# Revit family: NAU_Naughtone_Stng_LoungeChair_OakRockingBase3
name_source: partatom
category: Furniture
revit_build: Autodesk Revit 2016 (Build: 20150220_1215(x64)
units: mm (PartAtom-declared; Revit-internal decimal feet)

## family parameters
Always vertical = Yes
Cut with Voids When Loaded = No
OmniClass Number = 23.40.20.00
OmniClass Title = General Furniture and Specialties
Room Calculation Point = No
Shared = Yes
Work Plane-Based = No

## types (1)
- Standard
    AssetType = Movable
    BIMObjectName = NAU_Naughtone_Seating_LoungeChair_OakRockingBase
    Category = Pr_40_50_12 : Chairs, seats and benches
    Description = Always Lounge Chair with Oak Rocking Base with White Sub-Frame
    DurationUnit = year
    ExpectedLife = 5
    Finish = Fabric, Oak/Walnut Rocker, Black or White Metal Sub-Base
    IfcExportAs = IfcFurnishingElementType
    IfcExportType = CHAIR
    Keynote = Pr_40_50_12
    LegMaterial = NAU_Wood-Oak-Frame
    ManufacturerAddress = 201 Pannal Business Park, Station Road, Harrogate, HG3 1JL
    ManufacturerName = Naughtone
    ManufacturerURL = www.naughtone.com
    Material = Fabric, Solid Wood, Steel
    Model = ALLOBRK
    ModelNumber = ALLOBRK
    ModelReference = Always Lounge Chair with Oak Rocking Base with White Sub-Frame
    NBSDescription = Seating
    NBSReference = 45-35-72/352
    Name = Seating_LoungeChair_OakRockingBase_Naughtone
    NominalHeight = 930 mm  [stored 3.05118 ft]
    NominalLength = 790 mm  [stored 2.59186 ft]
    NominalWidth = 815 mm  [stored 2.67388 ft]
    ProductInformation = www.naughtone.com/portfolio-view/alwayslounge
    SeatMaterial = NAU_Wood-Oak-Frame
    Shape = Rectangular
    Size = 790 x 815 x 930mm
    SustainabilityPerformance = FSC certifeied, SCS indoor advantage gold
    URL = www.naughtone.com
    Uniclass2015Code = Pr_40_50_12
    Uniclass2015Title = Chairs, seats and benches
    Uniclass2015Version = Products v1.10
    Version = 1
    WarrantyDescription = 5 Years
    WarrantyDurationLabor = 5
    WarrantyDurationParts = 5
    WarrantyDurationUnit = year

note: [stored X ft] marks values corroborated as IEEE doubles in the binary element streams (Revit-internal decimal feet)

## geometry (parser evidence)
native form markers: Sweep x5
no freeform markers — native parametric forms only
